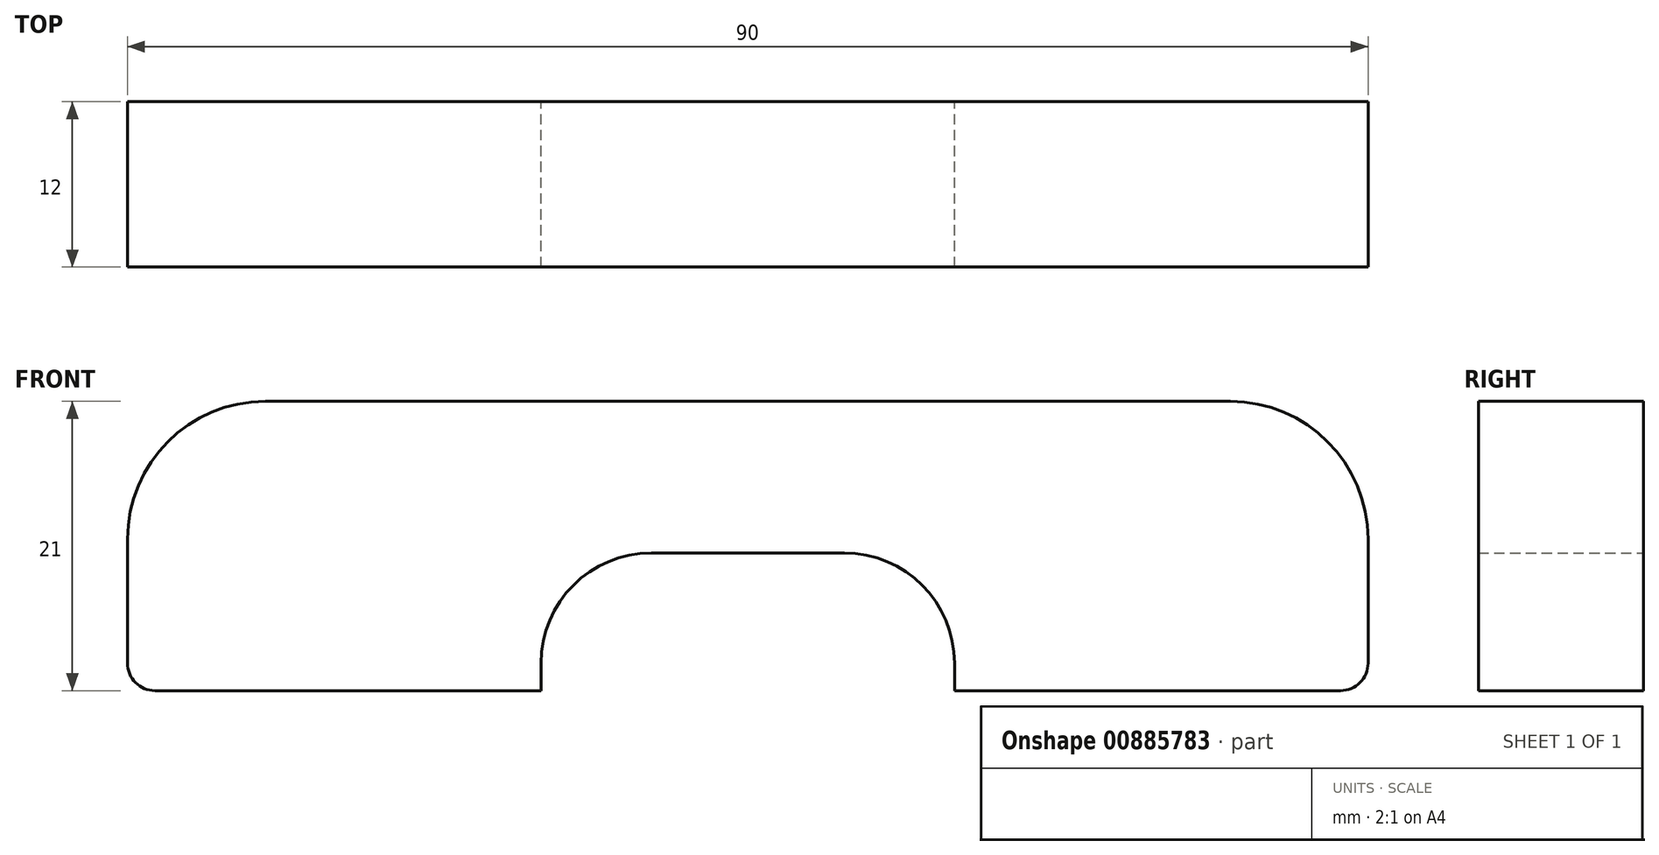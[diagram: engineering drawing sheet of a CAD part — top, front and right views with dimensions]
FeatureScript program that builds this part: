
annotation { "Feature Type Name" : "Feature", "Feature Type Description" : "" }
export const myFeature = defineFeature(function(context is Context, id is Id, definition is map)
    precondition{}
    {
        {
            var Q0;
            Q0=qCreatedBy(makeId("Front.planeOp"),FACE);
            var sketch = newSketch(context, id + "F0", { "sketchPlane" : qUnion([Q0])});
            skLineSegment(sketch, "E0", {"start": v(10, 0) * mm, "end": v(80, 0) * mm});
            skLineSegment(sketch, "E1", {"start": v(90, -10) * mm, "end": v(90, -19) * mm});
            skLineSegment(sketch, "E2", {"start": v(88, -21) * mm, "end": v(60, -21) * mm});
            skLineSegment(sketch, "E3", {"start": v(60, -21) * mm, "end": v(60, -19) * mm});
            skLineSegment(sketch, "E4", {"start": v(52, -11) * mm, "end": v(38, -11) * mm});
            skLineSegment(sketch, "E5", {"start": v(30, -19) * mm, "end": v(30, -21) * mm});
            skLineSegment(sketch, "E6", {"start": v(30, -21) * mm, "end": v(2, -21) * mm});
            skLineSegment(sketch, "E7", {"start": v(0, -19) * mm, "end": v(0, -10) * mm});
            skPoint(sketch, "E8.visualSharp", {"position": v(0, 0) * mm});
            skArc(sketch, "E8.filletArc", {"start": v(10, 0) * mm, "mid": v(2.93, -2.93) * mm, "end": v(0, -10) * mm});
            skPoint(sketch, "E9.visualSharp", {"position": v(90, 0) * mm});
            skArc(sketch, "E9.filletArc", {"start": v(90, -10) * mm, "mid": v(87.07, -2.93) * mm, "end": v(80, 0) * mm});
            skPoint(sketch, "E10.visualSharp", {"position": v(60, -11) * mm});
            skArc(sketch, "E10.filletArc", {"start": v(60, -19) * mm, "mid": v(57.66, -13.34) * mm, "end": v(52, -11) * mm});
            skPoint(sketch, "E11.visualSharp", {"position": v(30, -11) * mm});
            skArc(sketch, "E11.filletArc", {"start": v(38, -11) * mm, "mid": v(32.34, -13.34) * mm, "end": v(30, -19) * mm});
            skPoint(sketch, "E12.visualSharp", {"position": v(0, -21) * mm});
            skArc(sketch, "E12.filletArc", {"start": v(0, -19) * mm, "mid": v(0.59, -20.41) * mm, "end": v(2, -21) * mm});
            skPoint(sketch, "E13.visualSharp", {"position": v(90, -21) * mm});
            skArc(sketch, "E13.filletArc", {"start": v(88, -21) * mm, "mid": v(89.41, -20.41) * mm, "end": v(90, -19) * mm});
            skLineSegment(sketch, "E14", {"start": v(45, 0) * mm, "end": v(45, -5.5) * mm, "construction": true});
            skLineSegment(sketch, "E15", {"start": v(45, -5.5) * mm, "end": v(50, -5.5) * mm, "construction": true});
            skLineSegment(sketch, "E16", {"start": v(45, -5.5) * mm, "end": v(40, -5.5) * mm, "construction": true});
            skLineSegment(sketch, "E17", {"start": v(50, -5.5) * mm, "end": v(79, -5.5) * mm});
            skLineSegment(sketch, "E18", {"start": v(88, -21) * mm, "end": v(85, -21) * mm, "construction": true});
            skLineSegment(sketch, "E19", {"start": v(85, -21) * mm, "end": v(85, -16) * mm, "construction": true});
            skLineSegment(sketch, "E20", {"start": v(85, -16) * mm, "end": v(85, -11.5) * mm});
            skPoint(sketch, "E21.visualSharp", {"position": v(85, -5.5) * mm});
            skArc(sketch, "E21.filletArc", {"start": v(85, -11.5) * mm, "mid": v(83.24, -7.26) * mm, "end": v(79, -5.5) * mm});
            skLineSegment(sketch, "E22.MirrorCS", {"start": v(40, -5.5) * mm, "end": v(11, -5.5) * mm});
            skArc(sketch, "E23.MirrorCS", {"start": v(5, -11.5) * mm, "mid": v(6.76, -7.26) * mm, "end": v(11, -5.5) * mm});
            skLineSegment(sketch, "E24.MirrorCS", {"start": v(5, -16) * mm, "end": v(5, -11.5) * mm});
            skSolve(sketch);
        }
        {
            var Q0;
            Q0 = qSketchRegion(id + "F0", true);
            extrude(context, id + "F1", {"entities" : qUnion([Q0]), "depth" : 12 * mm, "offsetDistance" : 25 * mm});
        }
    });
